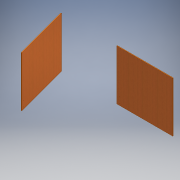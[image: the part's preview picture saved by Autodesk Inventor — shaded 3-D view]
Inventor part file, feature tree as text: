
AUTODESK INVENTOR PART (.ipt)
format: ipt  version: 2016 (Build 200138000, 138)  size: 175,616 bytes
history: native  units: mm
features: extrude x4, sketch x4, projected_geometry x2, plane x1
ambient origin geometry x8: Origin, YZ Plane, XZ Plane, XY Plane, X Axis, Y Axis, Z Axis, Center Point
bodies: Solid1 (feature_tree)
feature tree (11):
  plane  "Plano de trabajo4"
  extrude  "Extrusión8"  Depth=996.666667mm
  extrude  "Extrusión9"  TaperAngle=0.0deg  [1 undecoded]
  extrude  "Extrusión10"  Depth=80.0mm
  extrude  "Extrusión11"  Depth=730.0mm
  sketch  "Boceto8"  dims[d38=290.0mm d39=996.666667mm]
  sketch  "Boceto9"  dims[d40=10.0mm d42=0.0mm]
  projected_geometry  "Contorno proyectado7"
  sketch  "Boceto10"  dims[d43=49.833333mm d44=80.0mm]
  sketch  "Boceto11"  dims[d45=6.0mm d46=50.0mm d47=740.0mm d48=0.0mm d49=996.666667mm d50=996.666667mm d52=10.0mm d53=996.666667mm d54=730.0mm d55=0.0mm d56=49.833333mm d57=80.0mm d58=6.0mm d59=50.0mm d60=730.0mm d61=0.0mm]
  projected_geometry  "Contorno proyectado8"
note: 1 required parameter value undecoded (feature->parameter linkage not recoverable at this tier; creation-order binding heuristic only, values carry confidence <= 0.55)
